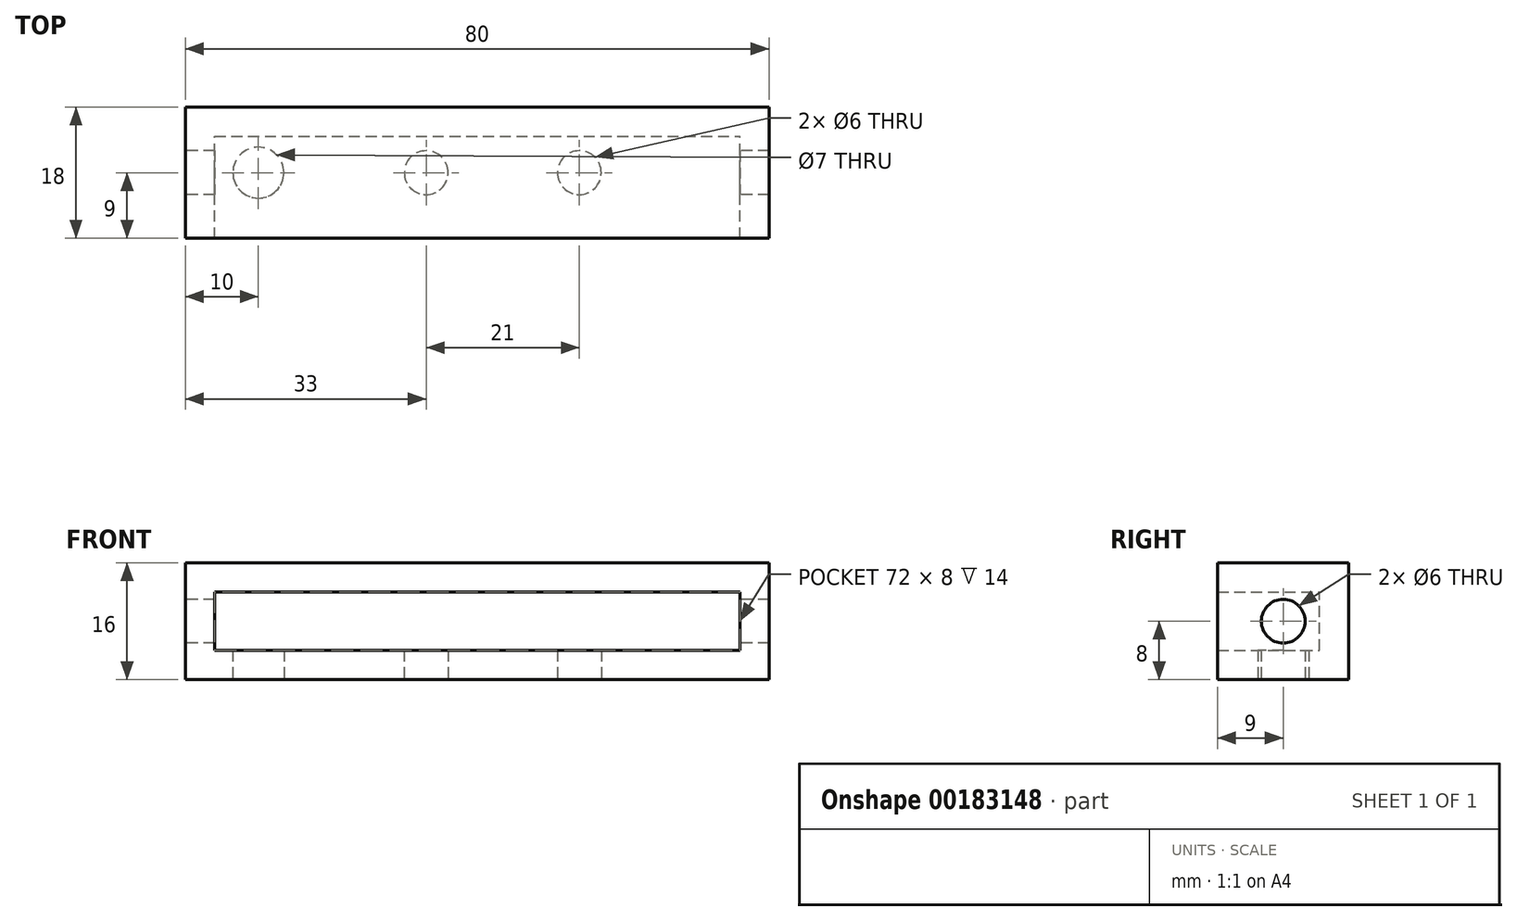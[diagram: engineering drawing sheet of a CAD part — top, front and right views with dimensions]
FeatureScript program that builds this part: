
annotation { "Feature Type Name" : "Feature", "Feature Type Description" : "" }
export const myFeature = defineFeature(function(context is Context, id is Id, definition is map)
    precondition{}
    {
        {
            var Q0;
            Q0=qCreatedBy(makeId("Front.planeOp"),FACE);
            var sketch = newSketch(context, id + "F0", { "sketchPlane" : qUnion([Q0])});
            skLineSegment(sketch, "E0.bottom", {"start": v(0, 0) * mm, "end": v(80, 0) * mm});
            skLineSegment(sketch, "E0.top", {"start": v(0, 16) * mm, "end": v(80, 16) * mm});
            skLineSegment(sketch, "E0.left", {"start": v(0, 0) * mm, "end": v(0, 16) * mm});
            skLineSegment(sketch, "E0.right", {"start": v(80, 0) * mm, "end": v(80, 16) * mm});
            skLineSegment(sketch, "E1.0", {"start": v(4, 4) * mm, "end": v(76, 4) * mm});
            skLineSegment(sketch, "E1.1", {"start": v(4, 4) * mm, "end": v(4, 12) * mm});
            skLineSegment(sketch, "E1.2", {"start": v(4, 12) * mm, "end": v(76, 12) * mm});
            skLineSegment(sketch, "E1.3", {"start": v(76, 4) * mm, "end": v(76, 12) * mm});
            skSolve(sketch);
        }
        {
            var Q0;
            Q0=makeQuery(id+"F0.imprint","IMPRINT",FACE,{"disambiguationData":[TD([[makeQuery(id+"F0.imprint","IMPRINT",EDGE,{"derivedFrom":sQuery(id+"F0.wireOp",EDGE,"E0.bottom")}),1.0]])]});
            extrude(context, id + "F1", {"entities" : qUnion([Q0]), "depth" : 18 * mm});
        }
        {
            var Q0;
            Q0=makeQuery(id+"F1.opExtrude","SWEPT_FACE",FACE,{"disambiguationData":[OSD([sQuery(id+"F0.wireOp",EDGE,"E0.left")])]});
            var sketch = newSketch(context, id + "F2", { "sketchPlane" : qUnion([Q0])});
            skCircle(sketch, "E2", {"center": v(9, 8) * mm, "radius": 3 * mm});
            skPoint(sketch, "E2.centerSnap0", {"position": v(0, 8) * mm});
            skPoint(sketch, "E2.centerSnap1", {"position": v(9, 16) * mm});
            skSolve(sketch);
        }
        {
            var Q0;
            Q0=makeQuery(id+"F2.imprint","IMPRINT",FACE,{"disambiguationData":[TD([[makeQuery(id+"F2.imprint","IMPRINT",EDGE,{"derivedFrom":sQuery(id+"F2.wireOp",EDGE,"E2")}),1.0]])]});
            extrude(context, id + "F3", {"entities" : qUnion([Q0]), "operationType" : NewBodyOperationType.REMOVE, "oppositeDirection" : true, "depth" : 80 * mm});
        }
        {
            var Q0;
            Q0=makeQuery(id+"F0.imprint","IMPRINT",FACE,{"disambiguationData":[TD([[makeQuery(id+"F0.imprint","IMPRINT",EDGE,{"derivedFrom":sQuery(id+"F0.wireOp",EDGE,"E1.0")}),1.0]])]});
            extrude(context, id + "F4", {"entities" : qUnion([Q0]), "operationType" : NewBodyOperationType.ADD, "depth" : 4 * mm});
        }
        {
            var Q0;
            Q0=makeQuery(id+"F1.opExtrude","SWEPT_FACE",FACE,{"disambiguationData":[OSD([sQuery(id+"F0.wireOp",EDGE,"E0.bottom")])]});
            var sketch = newSketch(context, id + "F5", { "sketchPlane" : qUnion([Q0])});
            skLineSegment(sketch, "E3", {"start": v(0, 9) * mm, "end": v(80, 9) * mm, "construction": true});
            skCircle(sketch, "E4", {"center": v(33, 9) * mm, "radius": 3 * mm});
            skCircle(sketch, "E5", {"center": v(54, 9) * mm, "radius": 3 * mm});
            skCircle(sketch, "E6", {"center": v(10, 9) * mm, "radius": 3.5 * mm});
            skSolve(sketch);
        }
        {
            var Q0;
            Q0=makeQuery(id+"F5.imprint","IMPRINT",FACE,{"disambiguationData":[TD([[makeQuery(id+"F5.imprint","IMPRINT",EDGE,{"derivedFrom":sQuery(id+"F5.wireOp",EDGE,"E6")}),1.0]])]});
            var Q1;
            Q1=makeQuery(id+"F5.imprint","IMPRINT",FACE,{"disambiguationData":[TD([[makeQuery(id+"F5.imprint","IMPRINT",EDGE,{"derivedFrom":sQuery(id+"F5.wireOp",EDGE,"E4")}),1.0]])]});
            var Q2;
            Q2=makeQuery(id+"F5.imprint","IMPRINT",FACE,{"disambiguationData":[TD([[makeQuery(id+"F5.imprint","IMPRINT",EDGE,{"derivedFrom":sQuery(id+"F5.wireOp",EDGE,"E5")}),1.0]])]});
            extrude(context, id + "F6", {"entities" : qUnion([Q0, Q1, Q2]), "operationType" : NewBodyOperationType.REMOVE, "oppositeDirection" : true, "depth" : 5 * mm});
        }
    });
